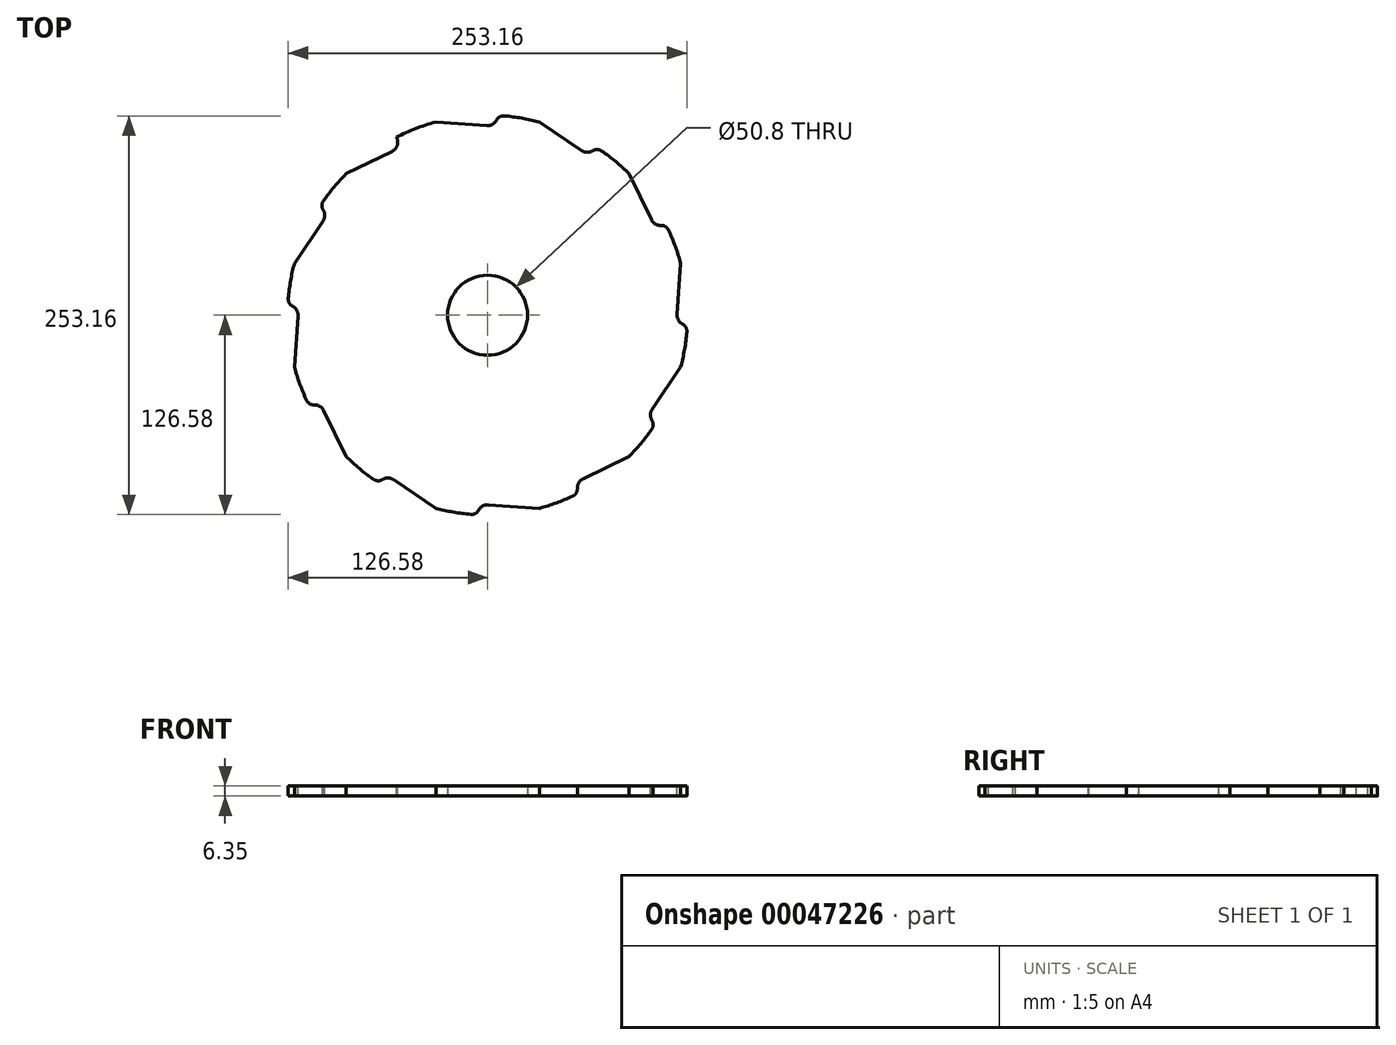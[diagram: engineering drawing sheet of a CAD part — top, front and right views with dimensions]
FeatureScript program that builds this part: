
annotation { "Feature Type Name" : "Feature", "Feature Type Description" : "" }
export const myFeature = defineFeature(function(context is Context, id is Id, definition is map)
    precondition{}
    {
        {
            var Q0;
            Q0=qCreatedBy(makeId("Top.planeOp"),FACE);
            var sketch = newSketch(context, id + "F0", { "sketchPlane" : qUnion([Q0])});
            skLineSegment(sketch, "E0", {"start": v(0, 0) * mm, "end": v(0, 131.88) * mm, "construction": true});
            skCircle(sketch, "E1", {"center": v(0, 0) * mm, "radius": 127 * mm});
            skCircle(sketch, "E2", {"center": v(0, 0) * mm, "radius": 25.4 * mm});
            skSolve(sketch);
        }
        {
            var Q0;
            Q0 = qSketchRegion(id + "F0", true);
            extrude(context, id + "F1", {"entities" : qUnion([Q0]), "depth" : 6.35 * mm});
        }
        {
            var Q0;
            Q0=makeQuery(id+"F1.opExtrude","CAP_FACE",FACE,{"disambiguationData":[OSD([sQuery(id+"F0.wireOp",EDGE,"E1"),sQuery(id+"F0.wireOp",EDGE,"E2")])],"isStart":false});
            var sketch = newSketch(context, id + "F2", { "sketchPlane" : qUnion([Q0])});
            skLineSegment(sketch, "E3", {"start": v(0, 0) * mm, "end": v(0, 127) * mm, "construction": true});
            skArc(sketch, "E4", {"start": v(6.35, 126.84) * mm, "mid": v(4.37, 122.13) * mm, "end": v(-0.44, 120.41) * mm});
            skLineSegment(sketch, "E5", {"start": v(-0.44, 120.41) * mm, "end": v(-32.87, 122.67) * mm});
            skArc(sketch, "E6", {"start": v(6.35, 126.84) * mm, "mid": v(-13.42, 126.29) * mm, "end": v(-32.87, 122.67) * mm});
            skLineSegment(sketch, "E7", {"start": v(-32.87, 122.67) * mm, "end": v(0, 0) * mm, "construction": true});
            skArc(sketch, "E8.1.0", {"start": v(-57.92, 113.02) * mm, "mid": v(-74.77, 102.66) * mm, "end": v(-89.8, 89.8) * mm});
            skLineSegment(sketch, "E8.1.1", {"start": v(-60.59, 104.06) * mm, "end": v(-89.8, 89.8) * mm});
            skArc(sketch, "E8.1.2", {"start": v(-57.92, 113.02) * mm, "mid": v(-57.29, 107.95) * mm, "end": v(-60.59, 104.06) * mm});
            skArc(sketch, "E8.2.0", {"start": v(-106.67, 68.92) * mm, "mid": v(-116.08, 51.52) * mm, "end": v(-122.67, 32.87) * mm});
            skLineSegment(sketch, "E8.2.1", {"start": v(-104.5, 59.82) * mm, "end": v(-122.67, 32.87) * mm});
            skArc(sketch, "E8.2.2", {"start": v(-106.67, 68.92) * mm, "mid": v(-103.59, 64.85) * mm, "end": v(-104.5, 59.82) * mm});
            skArc(sketch, "E8.3.0", {"start": v(-126.84, 6.35) * mm, "mid": v(-126.29, -13.42) * mm, "end": v(-122.67, -32.87) * mm});
            skLineSegment(sketch, "E8.3.1", {"start": v(-120.41, -0.44) * mm, "end": v(-122.67, -32.87) * mm});
            skArc(sketch, "E8.3.2", {"start": v(-126.84, 6.35) * mm, "mid": v(-122.13, 4.37) * mm, "end": v(-120.41, -0.44) * mm});
            skArc(sketch, "E8.4.0", {"start": v(-113.02, -57.92) * mm, "mid": v(-102.66, -74.77) * mm, "end": v(-89.8, -89.8) * mm});
            skLineSegment(sketch, "E8.4.1", {"start": v(-104.06, -60.59) * mm, "end": v(-89.8, -89.8) * mm});
            skArc(sketch, "E8.4.2", {"start": v(-113.02, -57.92) * mm, "mid": v(-107.95, -57.29) * mm, "end": v(-104.06, -60.59) * mm});
            skArc(sketch, "E8.5.0", {"start": v(-68.92, -106.67) * mm, "mid": v(-51.52, -116.08) * mm, "end": v(-32.87, -122.67) * mm});
            skLineSegment(sketch, "E8.5.1", {"start": v(-59.82, -104.5) * mm, "end": v(-32.87, -122.67) * mm});
            skArc(sketch, "E8.5.2", {"start": v(-68.92, -106.67) * mm, "mid": v(-64.85, -103.59) * mm, "end": v(-59.82, -104.5) * mm});
            skArc(sketch, "E8.6.0", {"start": v(-6.35, -126.84) * mm, "mid": v(13.42, -126.29) * mm, "end": v(32.87, -122.67) * mm});
            skLineSegment(sketch, "E8.6.1", {"start": v(0.44, -120.41) * mm, "end": v(32.87, -122.67) * mm});
            skArc(sketch, "E8.6.2", {"start": v(-6.35, -126.84) * mm, "mid": v(-4.37, -122.13) * mm, "end": v(0.44, -120.41) * mm});
            skArc(sketch, "E8.7.0", {"start": v(57.92, -113.02) * mm, "mid": v(74.77, -102.66) * mm, "end": v(89.8, -89.8) * mm});
            skLineSegment(sketch, "E8.7.1", {"start": v(60.59, -104.06) * mm, "end": v(89.8, -89.8) * mm});
            skArc(sketch, "E8.7.2", {"start": v(57.92, -113.02) * mm, "mid": v(57.29, -107.95) * mm, "end": v(60.59, -104.06) * mm});
            skArc(sketch, "E8.8.0", {"start": v(106.67, -68.92) * mm, "mid": v(116.08, -51.52) * mm, "end": v(122.67, -32.87) * mm});
            skLineSegment(sketch, "E8.8.1", {"start": v(104.5, -59.82) * mm, "end": v(122.67, -32.87) * mm});
            skArc(sketch, "E8.8.2", {"start": v(106.67, -68.92) * mm, "mid": v(103.59, -64.85) * mm, "end": v(104.5, -59.82) * mm});
            skArc(sketch, "E8.9.0", {"start": v(126.84, -6.35) * mm, "mid": v(126.29, 13.42) * mm, "end": v(122.67, 32.87) * mm});
            skLineSegment(sketch, "E8.9.1", {"start": v(120.41, 0.44) * mm, "end": v(122.67, 32.87) * mm});
            skArc(sketch, "E8.9.2", {"start": v(126.84, -6.35) * mm, "mid": v(122.13, -4.37) * mm, "end": v(120.41, 0.44) * mm});
            skArc(sketch, "E8.10.0", {"start": v(113.02, 57.92) * mm, "mid": v(102.66, 74.77) * mm, "end": v(89.8, 89.8) * mm});
            skLineSegment(sketch, "E8.10.1", {"start": v(104.06, 60.59) * mm, "end": v(89.8, 89.8) * mm});
            skArc(sketch, "E8.10.2", {"start": v(113.02, 57.92) * mm, "mid": v(107.95, 57.29) * mm, "end": v(104.06, 60.59) * mm});
            skArc(sketch, "E8.11.0", {"start": v(68.92, 106.67) * mm, "mid": v(51.52, 116.08) * mm, "end": v(32.87, 122.67) * mm});
            skLineSegment(sketch, "E8.11.1", {"start": v(59.82, 104.5) * mm, "end": v(32.87, 122.67) * mm});
            skArc(sketch, "E8.11.2", {"start": v(68.92, 106.67) * mm, "mid": v(64.85, 103.59) * mm, "end": v(59.82, 104.5) * mm});
            skLineSegment(sketch, "E8.anchor1", {"start": v(0, 0) * mm, "end": v(0, 0) * mm});
            skLineSegment(sketch, "E8.anchor2", {"start": v(0, 0) * mm, "end": v(0, 0) * mm});
            skSolve(sketch);
        }
        {
            var Q0;
            Q0 = qSketchRegion(id + "F2", true);
            extrude(context, id + "F3", {"entities" : qUnion([Q0]), "operationType" : NewBodyOperationType.REMOVE, "endBound" : BoundingType.THROUGH_ALL, "oppositeDirection" : true, "depth" : 25.4 * mm});
        }
        {
            var Q0;
            Q0=makeQuery(id+"F3.boolean.opBoolean","COPY",EDGE,{"derivedFrom":makeQuery(id+"F3.opExtrude","SWEPT_EDGE",EDGE,{"disambiguationData":[OSD([sQuery(id+"F0.wireOp",EDGE,"E1"),sQuery(id+"F2.wireOp",EDGE,"E4"),sQuery(id+"F2.wireOp",EDGE,"E6")])]})});
            var Q1;
            Q1=makeQuery(id+"F3.boolean.opBoolean","COPY",EDGE,{"derivedFrom":makeQuery(id+"F3.opExtrude","SWEPT_EDGE",EDGE,{"disambiguationData":[OSD([sQuery(id+"F0.wireOp",EDGE,"E1"),sQuery(id+"F2.wireOp",EDGE,"E8.11.0"),sQuery(id+"F2.wireOp",EDGE,"E8.11.2")])]})});
            var Q2;
            Q2=makeQuery(id+"F3.boolean.opBoolean","COPY",EDGE,{"derivedFrom":makeQuery(id+"F3.opExtrude","SWEPT_EDGE",EDGE,{"disambiguationData":[OSD([sQuery(id+"F0.wireOp",EDGE,"E1"),sQuery(id+"F2.wireOp",EDGE,"E8.10.0"),sQuery(id+"F2.wireOp",EDGE,"E8.10.2")])]})});
            var Q3;
            Q3=makeQuery(id+"F3.boolean.opBoolean","COPY",EDGE,{"derivedFrom":makeQuery(id+"F3.opExtrude","SWEPT_EDGE",EDGE,{"disambiguationData":[OSD([sQuery(id+"F0.wireOp",EDGE,"E1"),sQuery(id+"F2.wireOp",EDGE,"E8.9.0"),sQuery(id+"F2.wireOp",EDGE,"E8.9.2")])]})});
            var Q4;
            Q4=makeQuery(id+"F3.boolean.opBoolean","COPY",EDGE,{"derivedFrom":makeQuery(id+"F3.opExtrude","SWEPT_EDGE",EDGE,{"disambiguationData":[OSD([sQuery(id+"F0.wireOp",EDGE,"E1"),sQuery(id+"F2.wireOp",EDGE,"E8.8.0"),sQuery(id+"F2.wireOp",EDGE,"E8.8.2")])]})});
            var Q5;
            Q5=makeQuery(id+"F3.boolean.opBoolean","COPY",EDGE,{"derivedFrom":makeQuery(id+"F3.opExtrude","SWEPT_EDGE",EDGE,{"disambiguationData":[OSD([sQuery(id+"F0.wireOp",EDGE,"E1"),sQuery(id+"F2.wireOp",EDGE,"E8.1.0"),sQuery(id+"F2.wireOp",EDGE,"E8.1.2")])]})});
            var Q6;
            Q6=makeQuery(id+"F3.boolean.opBoolean","COPY",EDGE,{"derivedFrom":makeQuery(id+"F3.opExtrude","SWEPT_EDGE",EDGE,{"disambiguationData":[OSD([sQuery(id+"F0.wireOp",EDGE,"E1"),sQuery(id+"F2.wireOp",EDGE,"E8.2.0"),sQuery(id+"F2.wireOp",EDGE,"E8.2.2")])]})});
            var Q7;
            Q7=makeQuery(id+"F3.boolean.opBoolean","COPY",EDGE,{"derivedFrom":makeQuery(id+"F3.opExtrude","SWEPT_EDGE",EDGE,{"disambiguationData":[OSD([sQuery(id+"F0.wireOp",EDGE,"E1"),sQuery(id+"F2.wireOp",EDGE,"E8.3.0"),sQuery(id+"F2.wireOp",EDGE,"E8.3.2")])]})});
            var Q8;
            Q8=makeQuery(id+"F3.boolean.opBoolean","COPY",EDGE,{"derivedFrom":makeQuery(id+"F3.opExtrude","SWEPT_EDGE",EDGE,{"disambiguationData":[OSD([sQuery(id+"F0.wireOp",EDGE,"E1"),sQuery(id+"F2.wireOp",EDGE,"E8.4.0"),sQuery(id+"F2.wireOp",EDGE,"E8.4.2")])]})});
            var Q9;
            Q9=makeQuery(id+"F3.boolean.opBoolean","COPY",EDGE,{"derivedFrom":makeQuery(id+"F3.opExtrude","SWEPT_EDGE",EDGE,{"disambiguationData":[OSD([sQuery(id+"F0.wireOp",EDGE,"E1"),sQuery(id+"F2.wireOp",EDGE,"E8.5.0"),sQuery(id+"F2.wireOp",EDGE,"E8.5.2")])]})});
            var Q10;
            Q10=makeQuery(id+"F3.boolean.opBoolean","COPY",EDGE,{"derivedFrom":makeQuery(id+"F3.opExtrude","SWEPT_EDGE",EDGE,{"disambiguationData":[OSD([sQuery(id+"F0.wireOp",EDGE,"E1"),sQuery(id+"F2.wireOp",EDGE,"E8.6.0"),sQuery(id+"F2.wireOp",EDGE,"E8.6.2")])]})});
            var Q11;
            Q11=makeQuery(id+"F3.boolean.opBoolean","COPY",EDGE,{"derivedFrom":makeQuery(id+"F3.opExtrude","SWEPT_EDGE",EDGE,{"disambiguationData":[OSD([sQuery(id+"F0.wireOp",EDGE,"E1"),sQuery(id+"F2.wireOp",EDGE,"E8.7.0"),sQuery(id+"F2.wireOp",EDGE,"E8.7.2")])]})});
            fillet(context, id + "F4", {"entities" : qUnion([Q0, Q1, Q2, Q3, Q4, Q5, Q6, Q7, Q8, Q9, Q10, Q11]), "radius" : 5.08 * mm, "tangentPropagation" : true, "allowEdgeOverflow" : false});
        }
    });
